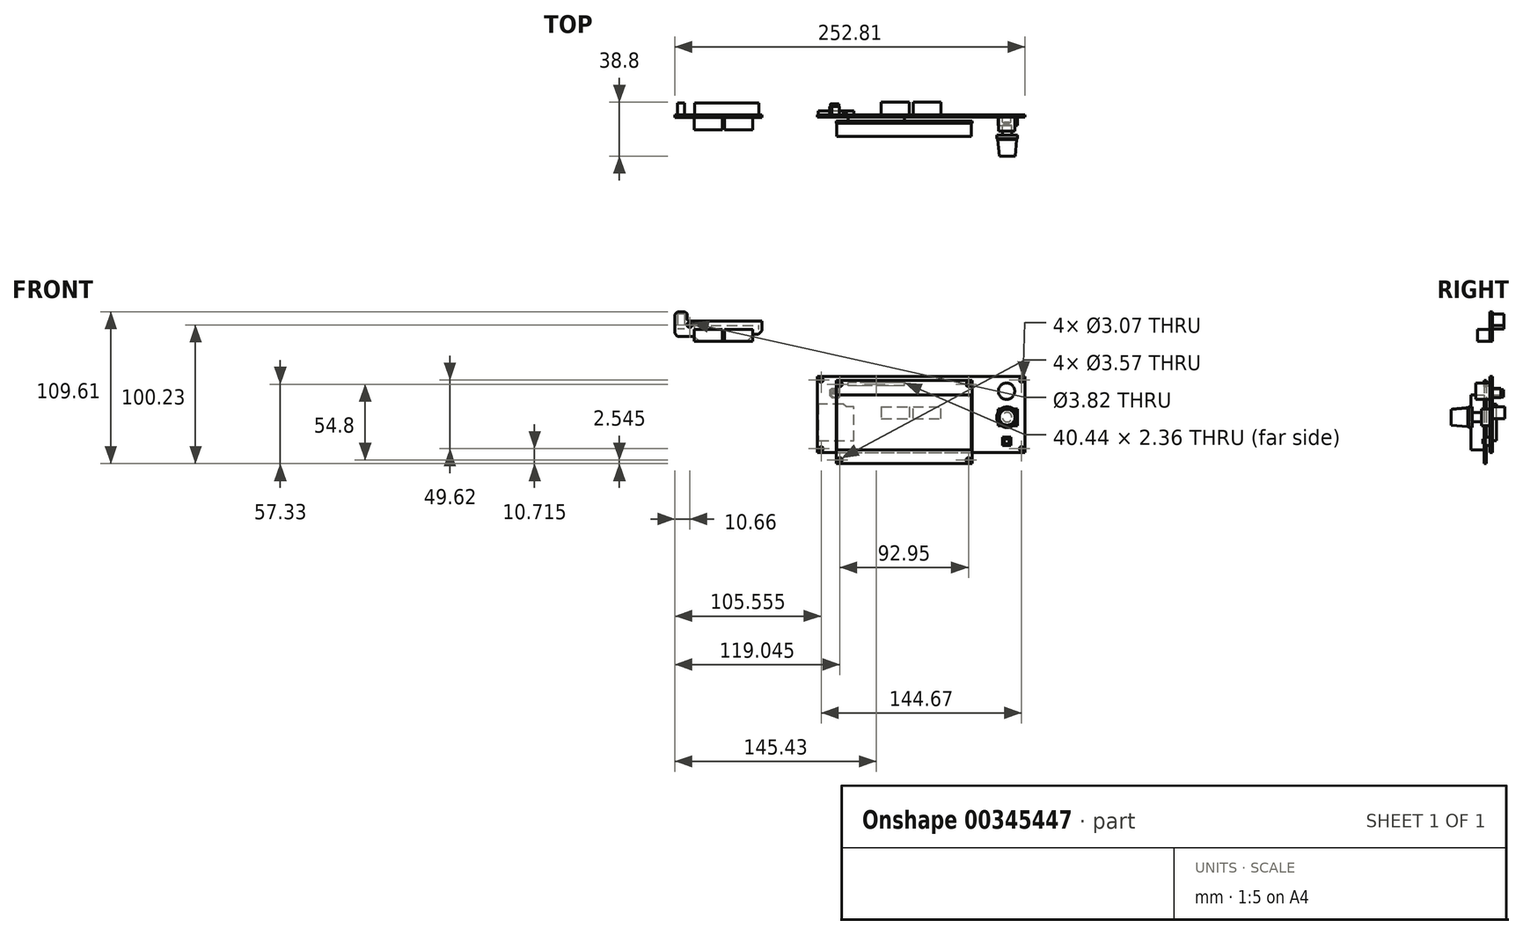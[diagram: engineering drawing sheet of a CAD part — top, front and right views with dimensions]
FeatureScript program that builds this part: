
annotation { "Feature Type Name" : "Feature", "Feature Type Description" : "" }
export const myFeature = defineFeature(function(context is Context, id is Id, definition is map)
    precondition{}
    {
        {
            var Q0;
            Q0=qCreatedBy(makeId("Front.planeOp"),FACE);
            var sketch = newSketch(context, id + "F0", { "sketchPlane" : qUnion([Q0])});
            skLineSegment(sketch, "E0.bottom", {"start": v(0, 0) * mm, "end": v(150.07, 0) * mm});
            skLineSegment(sketch, "E0.top", {"start": v(0, -55.1) * mm, "end": v(150.07, -55.1) * mm});
            skLineSegment(sketch, "E0.left", {"start": v(0, 0) * mm, "end": v(0, -55.1) * mm});
            skLineSegment(sketch, "E0.right", {"start": v(150.07, 0) * mm, "end": v(150.07, -55.1) * mm});
            skLineSegment(sketch, "E1", {"start": v(0, -2.7) * mm, "end": v(150.07, -2.7) * mm, "construction": true});
            skLineSegment(sketch, "E2", {"start": v(0, -52.33) * mm, "end": v(150.07, -52.32) * mm, "construction": true});
            skLineSegment(sketch, "E3", {"start": v(2.81, 0) * mm, "end": v(2.82, -55.1) * mm, "construction": true});
            skLineSegment(sketch, "E4", {"start": v(147.49, 0) * mm, "end": v(147.49, -55.1) * mm, "construction": true});
            skCircle(sketch, "E5", {"center": v(2.81, -2.7) * mm, "radius": 1.53 * mm});
            skCircle(sketch, "E6", {"center": v(2.81, -52.33) * mm, "radius": 1.53 * mm});
            skCircle(sketch, "E7", {"center": v(147.49, -2.7) * mm, "radius": 1.53 * mm});
            skCircle(sketch, "E8", {"center": v(147.49, -52.32) * mm, "radius": 1.53 * mm});
            skSolve(sketch);
        }
        {
            var Q0;
            Q0 = qSketchRegion(id + "F0", true);
            extrude(context, id + "F1", {"entities" : qUnion([Q0]), "depth" : 1.63 * mm});
        }
        {
            var Q0;
            Q0=makeQuery(id+"F1.opExtrude","CAP_FACE",FACE,{"disambiguationData":[OSD([sQuery(id+"F0.wireOp",EDGE,"E0.bottom"),sQuery(id+"F0.wireOp",EDGE,"E0.top"),sQuery(id+"F0.wireOp",EDGE,"E0.left"),sQuery(id+"F0.wireOp",EDGE,"E0.right")])],"isStart":false});
            cPlane(context, id + "F2", {"entities" : qUnion([Q0]), "cplaneType" : CPlaneType.OFFSET, "offset" : 2.7 * mm, "width" : 150 * mm, "height" : 150 * mm});
        }
        {
            var Q0;
            Q0=qCreatedBy(id+"F2.planeOp",FACE);
            var sketch = newSketch(context, id + "F3", { "sketchPlane" : qUnion([Q0])});
            skLineSegment(sketch, "E9.bottom", {"start": v(13.62, -3.08) * mm, "end": v(111.77, -3.08) * mm});
            skLineSegment(sketch, "E9.top", {"start": v(13.62, -63.04) * mm, "end": v(111.77, -63.04) * mm});
            skLineSegment(sketch, "E9.left", {"start": v(13.62, -3.08) * mm, "end": v(13.62, -63.04) * mm});
            skLineSegment(sketch, "E9.right", {"start": v(111.77, -3.08) * mm, "end": v(111.77, -63.04) * mm});
            skLineSegment(sketch, "E10.bottom", {"start": v(16.3, -5.7) * mm, "end": v(109.26, -5.7) * mm, "construction": true});
            skLineSegment(sketch, "E10.top", {"start": v(16.3, -60.5) * mm, "end": v(109.26, -60.5) * mm, "construction": true});
            skLineSegment(sketch, "E10.left", {"start": v(16.3, -5.7) * mm, "end": v(16.3, -60.5) * mm, "construction": true});
            skLineSegment(sketch, "E10.right", {"start": v(109.26, -5.7) * mm, "end": v(109.26, -60.5) * mm, "construction": true});
            skCircle(sketch, "E11", {"center": v(16.3, -5.7) * mm, "radius": 1.78 * mm});
            skCircle(sketch, "E12", {"center": v(109.26, -5.7) * mm, "radius": 1.78 * mm});
            skCircle(sketch, "E13", {"center": v(16.3, -60.5) * mm, "radius": 1.78 * mm});
            skCircle(sketch, "E14", {"center": v(109.26, -60.5) * mm, "radius": 1.78 * mm});
            skSolve(sketch);
        }
        {
            var Q0;
            Q0 = qSketchRegion(id + "F3", true);
            extrude(context, id + "F4", {"entities" : qUnion([Q0]), "depth" : 1.62 * mm});
        }
        {
            var Q0;
            Q0=makeQuery(id+"F4.opExtrude","CAP_FACE",FACE,{"disambiguationData":[OSD([sQuery(id+"F3.wireOp",EDGE,"E9.bottom"),sQuery(id+"F3.wireOp",EDGE,"E9.top"),sQuery(id+"F3.wireOp",EDGE,"E9.left"),sQuery(id+"F3.wireOp",EDGE,"E9.right")])],"isStart":false});
            var sketch = newSketch(context, id + "F5", { "sketchPlane" : qUnion([Q0])});
            skLineSegment(sketch, "E15", {"start": v(62.7, -3.08) * mm, "end": v(62.7, -63.04) * mm, "construction": true});
            skLineSegment(sketch, "E16.bottom", {"start": v(14.18, -13.36) * mm, "end": v(111.2, -13.36) * mm});
            skLineSegment(sketch, "E16.top", {"start": v(14.19, -53.18) * mm, "end": v(111.2, -53.18) * mm});
            skLineSegment(sketch, "E16.left", {"start": v(14.19, -13.36) * mm, "end": v(14.19, -53.18) * mm});
            skLineSegment(sketch, "E16.right", {"start": v(111.2, -13.36) * mm, "end": v(111.2, -53.18) * mm});
            skCircle(sketch, "E17", {"center": v(62.7, -33.06) * mm, "radius": 48.5 * mm, "construction": true});
            skSolve(sketch);
        }
        {
            var Q0;
            Q0 = qSketchRegion(id + "F5", true);
            extrude(context, id + "F6", {"entities" : qUnion([Q0]), "operationType" : NewBodyOperationType.ADD, "depth" : 9.45 * mm});
        }
        {
            var Q0;
            Q0=makeQuery(id+"F1.opExtrude","CAP_FACE",FACE,{"disambiguationData":[OSD([sQuery(id+"F0.wireOp",EDGE,"E0.bottom"),sQuery(id+"F0.wireOp",EDGE,"E0.top"),sQuery(id+"F0.wireOp",EDGE,"E0.left"),sQuery(id+"F0.wireOp",EDGE,"E0.right")])],"isStart":false});
            var sketch = newSketch(context, id + "F7", { "sketchPlane" : qUnion([Q0])});
            skLineSegment(sketch, "E18.bottom", {"start": v(133.8, -43.96) * mm, "end": v(139.76, -43.96) * mm});
            skLineSegment(sketch, "E18.top", {"start": v(133.8, -49.92) * mm, "end": v(139.76, -49.92) * mm});
            skLineSegment(sketch, "E18.left", {"start": v(133.8, -43.96) * mm, "end": v(133.8, -49.92) * mm});
            skLineSegment(sketch, "E18.right", {"start": v(139.76, -43.96) * mm, "end": v(139.76, -49.92) * mm});
            skCircle(sketch, "E19", {"center": v(136.78, -46.94) * mm, "radius": 2.98 * mm, "construction": true});
            skSolve(sketch);
        }
        {
            var Q0;
            Q0 = qSketchRegion(id + "F7", true);
            extrude(context, id + "F8", {"entities" : qUnion([Q0]), "operationType" : NewBodyOperationType.ADD, "depth" : 3.55 * mm});
        }
        {
            var Q0;
            Q0=makeQuery(id+"F8.opExtrude","CAP_FACE",FACE,{"disambiguationData":[OSD([sQuery(id+"F7.wireOp",EDGE,"E18.bottom"),sQuery(id+"F7.wireOp",EDGE,"E18.top"),sQuery(id+"F7.wireOp",EDGE,"E18.left"),sQuery(id+"F7.wireOp",EDGE,"E18.right")])],"isStart":false});
            var sketch = newSketch(context, id + "F9", { "sketchPlane" : qUnion([Q0])});
            skLineSegment(sketch, "E20", {"start": v(133.8, -43.96) * mm, "end": v(139.76, -49.92) * mm, "construction": true});
            skCircle(sketch, "E21", {"center": v(136.78, -46.94) * mm, "radius": 1.76 * mm});
            skSolve(sketch);
        }
        {
            var Q0;
            Q0 = qSketchRegion(id + "F9", true);
            extrude(context, id + "F10", {"entities" : qUnion([Q0]), "operationType" : NewBodyOperationType.ADD, "depth" : 1.57 * mm});
        }
        {
            var Q0;
            Q0=makeQuery(id+"F1.opExtrude","CAP_FACE",FACE,{"disambiguationData":[OSD([sQuery(id+"F0.wireOp",EDGE,"E0.bottom"),sQuery(id+"F0.wireOp",EDGE,"E0.top"),sQuery(id+"F0.wireOp",EDGE,"E0.left"),sQuery(id+"F0.wireOp",EDGE,"E0.right"),sQuery(id+"F0.wireOp",EDGE,"E5"),sQuery(id+"F0.wireOp",EDGE,"E6"),sQuery(id+"F0.wireOp",EDGE,"E7"),sQuery(id+"F0.wireOp",EDGE,"E8")])],"isStart":false});
            var sketch = newSketch(context, id + "F11", { "sketchPlane" : qUnion([Q0])});
            skLineSegment(sketch, "E22.bottom", {"start": v(130.73, -23.6) * mm, "end": v(144.54, -23.6) * mm});
            skLineSegment(sketch, "E22.top", {"start": v(130.73, -35.51) * mm, "end": v(144.54, -35.51) * mm});
            skLineSegment(sketch, "E22.left", {"start": v(130.73, -23.6) * mm, "end": v(130.73, -35.51) * mm});
            skLineSegment(sketch, "E22.right", {"start": v(144.54, -23.6) * mm, "end": v(144.54, -35.51) * mm});
            skSolve(sketch);
        }
        {
            var Q0;
            Q0 = qSketchRegion(id + "F11", true);
            extrude(context, id + "F12", {"entities" : qUnion([Q0]), "operationType" : NewBodyOperationType.ADD, "depth" : 6.04 * mm});
        }
        {
            var Q0;
            Q0=makeQuery(id+"F12.opExtrude","CAP_FACE",FACE,{"disambiguationData":[OSD([sQuery(id+"F11.wireOp",EDGE,"E22.bottom"),sQuery(id+"F11.wireOp",EDGE,"E22.top"),sQuery(id+"F11.wireOp",EDGE,"E22.left"),sQuery(id+"F11.wireOp",EDGE,"E22.right")])],"isStart":false});
            var sketch = newSketch(context, id + "F13", { "sketchPlane" : qUnion([Q0])});
            skLineSegment(sketch, "E23", {"start": v(130.73, -29.55) * mm, "end": v(144.54, -29.55) * mm, "construction": true});
            skCircle(sketch, "E24", {"center": v(137.11, -29.55) * mm, "radius": 3.41 * mm});
            skSolve(sketch);
        }
        {
            var Q0;
            Q0 = qSketchRegion(id + "F13", true);
            extrude(context, id + "F14", {"entities" : qUnion([Q0]), "operationType" : NewBodyOperationType.ADD, "depth" : 6.86 * mm});
        }
        {
            var Q0;
            Q0=sQuery(id+"F13.wireOp",EDGE,"E23");
            cPoint(context, id + "F15", {"entities" : qUnion([Q0]), "parameter" : 0.5});
        }
        {
            var Q0;
            Q0=qCreatedBy(makeId("Top.planeOp"),FACE);
            var Q1;
            Q1 = qCreatedBy(id + "F15" ,VERTEX);
            cPlane(context, id + "F16", {"entities" : qUnion([Q0, Q1]), "cplaneType" : CPlaneType.PLANE_POINT, "offset" : 25 * mm, "width" : 150 * mm, "height" : 150 * mm});
        }
        {
            var Q0;
            Q0=qCreatedBy(id+"F16.planeOp",FACE);
            var sketch = newSketch(context, id + "F17", { "sketchPlane" : qUnion([Q0])});
            skLineSegment(sketch, "E25.0", {"start": v(140.52, -14.53) * mm, "end": v(133.7, -14.53) * mm, "construction": true});
            skLineSegment(sketch, "E26", {"start": v(137.11, -14.53) * mm, "end": v(137.11, -29.65) * mm});
            skLineSegment(sketch, "E27", {"start": v(137.11, -29.65) * mm, "end": v(142.84, -29.65) * mm});
            skLineSegment(sketch, "E28", {"start": v(142.84, -29.65) * mm, "end": v(143.96, -17.58) * mm});
            skLineSegment(sketch, "E29", {"start": v(143.96, -17.58) * mm, "end": v(144.6, -16.95) * mm});
            skLineSegment(sketch, "E30", {"start": v(144.6, -16.95) * mm, "end": v(144.6, -14.53) * mm});
            skLineSegment(sketch, "E31", {"start": v(144.6, -14.53) * mm, "end": v(137.11, -14.53) * mm});
            skSolve(sketch);
        }
        {
            var Q0;
            Q0 = qSketchRegion(id + "F17", true);
            var Q1;
            Q1=sQuery(id+"F17.wireOp",EDGE,"E26");
            revolve(context, id + "F18", {"operationType" : NewBodyOperationType.ADD, "entities" : qUnion([Q0]), "axis" : qUnion([Q1]), "revolveType" : RevolveType.FULL});
        }
        {
            var Q0;
            Q0=makeQuery(id+"F1.opExtrude","CAP_FACE",FACE,{"disambiguationData":[OSD([sQuery(id+"F0.wireOp",EDGE,"E0.bottom"),sQuery(id+"F0.wireOp",EDGE,"E0.top"),sQuery(id+"F0.wireOp",EDGE,"E0.left"),sQuery(id+"F0.wireOp",EDGE,"E0.right"),sQuery(id+"F0.wireOp",EDGE,"E5"),sQuery(id+"F0.wireOp",EDGE,"E6"),sQuery(id+"F0.wireOp",EDGE,"E7"),sQuery(id+"F0.wireOp",EDGE,"E8")])],"isStart":false});
            var sketch = newSketch(context, id + "F19", { "sketchPlane" : qUnion([Q0])});
            skCircle(sketch, "E32", {"center": v(136.68, -10.73) * mm, "radius": 5.9 * mm});
            skSolve(sketch);
        }
        {
            var Q0;
            Q0 = qSketchRegion(id + "F19", true);
            extrude(context, id + "F20", {"entities" : qUnion([Q0]), "operationType" : NewBodyOperationType.ADD, "depth" : 10.15 * mm});
        }
        {
            var Q0;
            Q0=makeQuery(id+"F1.opExtrude","CAP_FACE",FACE,{"disambiguationData":[OSD([sQuery(id+"F0.wireOp",EDGE,"E0.bottom"),sQuery(id+"F0.wireOp",EDGE,"E0.top"),sQuery(id+"F0.wireOp",EDGE,"E0.left"),sQuery(id+"F0.wireOp",EDGE,"E0.right"),sQuery(id+"F0.wireOp",EDGE,"E5"),sQuery(id+"F0.wireOp",EDGE,"E6"),sQuery(id+"F0.wireOp",EDGE,"E7"),sQuery(id+"F0.wireOp",EDGE,"E8")])],"isStart":true});
            var sketch = newSketch(context, id + "F21", { "sketchPlane" : qUnion([Q0])});
            skLineSegment(sketch, "E33", {"start": v(-0.8, -46.57) * mm, "end": v(-26.48, -46.57) * mm});
            skLineSegment(sketch, "E34", {"start": v(-26.48, -46.57) * mm, "end": v(-26.48, -22.15) * mm});
            skLineSegment(sketch, "E35", {"start": v(-26.48, -22.15) * mm, "end": v(-21.02, -22.15) * mm});
            skLineSegment(sketch, "E36", {"start": v(-21.02, -22.15) * mm, "end": v(-18.87, -20) * mm});
            skLineSegment(sketch, "E37", {"start": v(-18.87, -20) * mm, "end": v(-0.8, -20) * mm});
            skLineSegment(sketch, "E38", {"start": v(-0.8, -20) * mm, "end": v(-0.8, -46.57) * mm});
            skSolve(sketch);
        }
        {
            var Q0;
            Q0 = qSketchRegion(id + "F21", true);
            extrude(context, id + "F22", {"entities" : qUnion([Q0]), "operationType" : NewBodyOperationType.ADD, "depth" : 2.91 * mm});
        }
        {
            var Q0;
            Q0=makeQuery(id+"F1.opExtrude","CAP_FACE",FACE,{"disambiguationData":[OSD([sQuery(id+"F0.wireOp",EDGE,"E0.bottom"),sQuery(id+"F0.wireOp",EDGE,"E0.top"),sQuery(id+"F0.wireOp",EDGE,"E0.left"),sQuery(id+"F0.wireOp",EDGE,"E0.right"),sQuery(id+"F0.wireOp",EDGE,"E5"),sQuery(id+"F0.wireOp",EDGE,"E6"),sQuery(id+"F0.wireOp",EDGE,"E7"),sQuery(id+"F0.wireOp",EDGE,"E8")])],"isStart":true});
            var sketch = newSketch(context, id + "F23", { "sketchPlane" : qUnion([Q0])});
            skLineSegment(sketch, "E39", {"start": v(-15.96, -11.92) * mm, "end": v(-9.02, -11.92) * mm, "construction": true});
            skLineSegment(sketch, "E40", {"start": v(-9.02, -11.92) * mm, "end": v(-9.02, -10.05) * mm});
            skLineSegment(sketch, "E41", {"start": v(-9.02, -10.05) * mm, "end": v(-10.48, -8.6) * mm});
            skLineSegment(sketch, "E42", {"start": v(-10.48, -8.6) * mm, "end": v(-15.96, -8.6) * mm});
            skLineSegment(sketch, "E43", {"start": v(-15.96, -8.6) * mm, "end": v(-15.96, -11.92) * mm});
            skLineSegment(sketch, "E44.MirrorCS", {"start": v(-15.96, -15.25) * mm, "end": v(-15.96, -11.92) * mm});
            skLineSegment(sketch, "E45.MirrorCS", {"start": v(-10.48, -15.25) * mm, "end": v(-15.96, -15.25) * mm});
            skLineSegment(sketch, "E46.MirrorCS", {"start": v(-9.02, -13.78) * mm, "end": v(-10.49, -15.25) * mm});
            skLineSegment(sketch, "E47.MirrorCS", {"start": v(-9.02, -11.92) * mm, "end": v(-9.02, -13.78) * mm});
            skSolve(sketch);
        }
        {
            var Q0;
            Q0 = qSketchRegion(id + "F23", true);
            extrude(context, id + "F24", {"entities" : qUnion([Q0]), "operationType" : NewBodyOperationType.ADD, "depth" : 6.15 * mm});
        }
        {
            var Q0;
            Q0=makeQuery(id+"F24.opExtrude","CAP_FACE",FACE,{"disambiguationData":[OSD([sQuery(id+"F23.wireOp",EDGE,"E40"),sQuery(id+"F23.wireOp",EDGE,"E41"),sQuery(id+"F23.wireOp",EDGE,"E42"),sQuery(id+"F23.wireOp",EDGE,"E43"),sQuery(id+"F23.wireOp",EDGE,"E44.MirrorCS"),sQuery(id+"F23.wireOp",EDGE,"E45.MirrorCS"),sQuery(id+"F23.wireOp",EDGE,"E46.MirrorCS"),sQuery(id+"F23.wireOp",EDGE,"E47.MirrorCS")])],"isStart":false});
            var sketch = newSketch(context, id + "F25", { "sketchPlane" : qUnion([Q0])});
            skLineSegment(sketch, "E48.0", {"start": v(-15.96, -11.92) * mm, "end": v(-9.02, -11.92) * mm, "construction": true});
            skCircle(sketch, "E49", {"center": v(-12.5, -11.92) * mm, "radius": 3 * mm});
            skLineSegment(sketch, "E50.bottom", {"start": v(-14.72, -11.4) * mm, "end": v(-12.5, -11.4) * mm});
            skLineSegment(sketch, "E50.left", {"start": v(-14.72, -11.4) * mm, "end": v(-14.72, -11.92) * mm});
            skLineSegment(sketch, "E51", {"start": v(-12.5, -11.92) * mm, "end": v(-12.5, -8.91) * mm, "construction": true});
            skLineSegment(sketch, "E52", {"start": v(-12.5, -11.92) * mm, "end": v(-12.5, -14.93) * mm, "construction": true});
            skLineSegment(sketch, "E53", {"start": v(-14.25, -9.48) * mm, "end": v(-13.82, -9.48) * mm});
            skLineSegment(sketch, "E54", {"start": v(-13.82, -9.48) * mm, "end": v(-13.82, -10.03) * mm});
            skLineSegment(sketch, "E55", {"start": v(-13.82, -10.03) * mm, "end": v(-12.5, -10.03) * mm});
            skLineSegment(sketch, "E56.MirrorCS", {"start": v(-14.72, -12.45) * mm, "end": v(-12.5, -12.45) * mm});
            skLineSegment(sketch, "E57.MirrorCS", {"start": v(-14.72, -12.45) * mm, "end": v(-14.72, -11.92) * mm});
            skLineSegment(sketch, "E58.MirrorCS", {"start": v(-11.16, -10.03) * mm, "end": v(-12.5, -10.03) * mm});
            skLineSegment(sketch, "E59.MirrorCS", {"start": v(-11.16, -9.48) * mm, "end": v(-11.16, -10.03) * mm});
            skLineSegment(sketch, "E60.MirrorCS", {"start": v(-10.73, -9.48) * mm, "end": v(-11.16, -9.48) * mm});
            skLineSegment(sketch, "E61.MirrorCS", {"start": v(-10.27, -11.4) * mm, "end": v(-12.5, -11.4) * mm});
            skLineSegment(sketch, "E62.MirrorCS", {"start": v(-10.27, -11.4) * mm, "end": v(-10.27, -11.92) * mm});
            skLineSegment(sketch, "E63.MirrorCS", {"start": v(-10.27, -12.45) * mm, "end": v(-10.27, -11.92) * mm});
            skLineSegment(sketch, "E64.MirrorCS", {"start": v(-10.27, -12.45) * mm, "end": v(-12.5, -12.45) * mm});
            skSolve(sketch);
        }
        {
            var Q0;
            Q0=makeQuery(id+"F25.imprint","IMPRINT",FACE,{"disambiguationData":[TD([[makeQuery(id+"F25.imprint","IMPRINT",EDGE,{"derivedFrom":sQuery(id+"F25.wireOp",EDGE,"E50.bottom")}),1.0]])]});
            extrude(context, id + "F26", {"entities" : qUnion([Q0]), "operationType" : NewBodyOperationType.ADD, "depth" : 1.85 * mm});
        }
        {
            var Q0;
            Q0=makeQuery(id+"F1.opExtrude","CAP_FACE",FACE,{"disambiguationData":[OSD([sQuery(id+"F0.wireOp",EDGE,"E0.bottom"),sQuery(id+"F0.wireOp",EDGE,"E0.top"),sQuery(id+"F0.wireOp",EDGE,"E0.left"),sQuery(id+"F0.wireOp",EDGE,"E0.right"),sQuery(id+"F0.wireOp",EDGE,"E5"),sQuery(id+"F0.wireOp",EDGE,"E6"),sQuery(id+"F0.wireOp",EDGE,"E7"),sQuery(id+"F0.wireOp",EDGE,"E8")])],"isStart":true});
            var sketch = newSketch(context, id + "F27", { "sketchPlane" : qUnion([Q0])});
            skLineSegment(sketch, "E65.bottom", {"start": v(-46.17, -22) * mm, "end": v(-66.44, -22) * mm});
            skLineSegment(sketch, "E65.top", {"start": v(-46.17, -30.71) * mm, "end": v(-66.44, -30.71) * mm});
            skLineSegment(sketch, "E65.left", {"start": v(-46.17, -22) * mm, "end": v(-46.17, -30.71) * mm});
            skLineSegment(sketch, "E65.right", {"start": v(-66.44, -22) * mm, "end": v(-66.44, -30.71) * mm});
            skLineSegment(sketch, "E66.bottom", {"start": v(-69.19, -30.71) * mm, "end": v(-89.46, -30.71) * mm});
            skLineSegment(sketch, "E66.top", {"start": v(-69.19, -22) * mm, "end": v(-89.46, -22) * mm});
            skLineSegment(sketch, "E66.left", {"start": v(-69.19, -30.71) * mm, "end": v(-69.19, -22) * mm});
            skLineSegment(sketch, "E66.right", {"start": v(-89.46, -30.71) * mm, "end": v(-89.46, -22) * mm});
            skLineSegment(sketch, "E67", {"start": v(-69.19, -30.71) * mm, "end": v(-66.44, -30.71) * mm, "construction": true});
            skLineSegment(sketch, "E68", {"start": v(-66.44, -22) * mm, "end": v(-69.19, -22) * mm, "construction": true});
            skSolve(sketch);
        }
        {
            var Q0;
            Q0 = qSketchRegion(id + "F27", true);
            extrude(context, id + "F28", {"entities" : qUnion([Q0]), "operationType" : NewBodyOperationType.ADD, "depth" : 9.15 * mm});
        }
        {
            var Q0;
            Q0=qCreatedBy(makeId("Front.planeOp"),FACE);
            var sketch = newSketch(context, id + "F29", { "sketchPlane" : qUnion([Q0])});
            skLineSegment(sketch, "E69", {"start": v(-40, 40) * mm, "end": v(-92.4, 40) * mm});
            skLineSegment(sketch, "E70", {"start": v(-93.99, 41.6) * mm, "end": v(-93.99, 45.24) * mm});
            skLineSegment(sketch, "E71", {"start": v(-93.99, 45.24) * mm, "end": v(-95.32, 46.57) * mm});
            skLineSegment(sketch, "E72", {"start": v(-95.32, 46.57) * mm, "end": v(-100.78, 46.57) * mm});
            skLineSegment(sketch, "E73", {"start": v(-100.78, 46.57) * mm, "end": v(-102.74, 44.6) * mm});
            skLineSegment(sketch, "E74", {"start": v(-102.74, 44.6) * mm, "end": v(-102.74, 30.85) * mm});
            skLineSegment(sketch, "E75", {"start": v(-102.74, 30.85) * mm, "end": v(-100.78, 28.89) * mm});
            skLineSegment(sketch, "E76", {"start": v(-100.78, 28.89) * mm, "end": v(-88.78, 28.89) * mm});
            skLineSegment(sketch, "E77", {"start": v(-88.78, 28.89) * mm, "end": v(-85.05, 25.16) * mm});
            skLineSegment(sketch, "E78", {"start": v(-85.05, 25.16) * mm, "end": v(-50.73, 25.16) * mm});
            skLineSegment(sketch, "E79", {"start": v(-50.73, 25.16) * mm, "end": v(-45.51, 30.38) * mm});
            skLineSegment(sketch, "E80", {"start": v(-42.42, 30.38) * mm, "end": v(-40, 32.8) * mm});
            skLineSegment(sketch, "E81", {"start": v(-40, 32.8) * mm, "end": v(-40, 40) * mm});
            skLineSegment(sketch, "E82", {"start": v(-45.51, 30.38) * mm, "end": v(-42.42, 30.38) * mm});
            skLineSegment(sketch, "E83", {"start": v(-100.78, 46.57) * mm, "end": v(-100.78, 28.89) * mm, "construction": true});
            skPoint(sketch, "E84.visualSharp", {"position": v(-93.99, 40) * mm});
            skArc(sketch, "E84.filletArc", {"start": v(-94, 41.6) * mm, "mid": v(-93.52, 40.47) * mm, "end": v(-92.4, 40) * mm});
            skCircle(sketch, "E85", {"center": v(-92.08, 37.19) * mm, "radius": 1.91 * mm});
            skLineSegment(sketch, "E86", {"start": v(-93.99, 41.6) * mm, "end": v(-93.99, 28.89) * mm, "construction": true});
            skSolve(sketch);
        }
        {
            var Q0;
            Q0 = qSketchRegion(id + "F29", true);
            extrude(context, id + "F30", {"entities" : qUnion([Q0]), "depth" : 1.74 * mm});
        }
        {
            var Q0;
            Q0=makeQuery(id+"F30.opExtrude","CAP_FACE",FACE,{"disambiguationData":[OSD([sQuery(id+"F29.wireOp",EDGE,"E69"),sQuery(id+"F29.wireOp",EDGE,"E70"),sQuery(id+"F29.wireOp",EDGE,"E71"),sQuery(id+"F29.wireOp",EDGE,"E72"),sQuery(id+"F29.wireOp",EDGE,"E73"),sQuery(id+"F29.wireOp",EDGE,"E74"),sQuery(id+"F29.wireOp",EDGE,"E75"),sQuery(id+"F29.wireOp",EDGE,"E76"),sQuery(id+"F29.wireOp",EDGE,"E77"),sQuery(id+"F29.wireOp",EDGE,"E78"),sQuery(id+"F29.wireOp",EDGE,"E79"),sQuery(id+"F29.wireOp",EDGE,"E80"),sQuery(id+"F29.wireOp",EDGE,"E81"),sQuery(id+"F29.wireOp",EDGE,"E82"),sQuery(id+"F29.wireOp",EDGE,"E84.filletArc"),sQuery(id+"F29.wireOp",EDGE,"E85")])],"isStart":false});
            var sketch = newSketch(context, id + "F31", { "sketchPlane" : qUnion([Q0])});
            skLineSegment(sketch, "E87.bottom", {"start": v(-68.54, 25.16) * mm, "end": v(-88.78, 25.16) * mm});
            skLineSegment(sketch, "E87.top", {"start": v(-68.54, 33.78) * mm, "end": v(-88.78, 33.78) * mm});
            skLineSegment(sketch, "E87.left", {"start": v(-68.54, 25.16) * mm, "end": v(-68.54, 33.78) * mm});
            skLineSegment(sketch, "E87.right", {"start": v(-88.78, 25.16) * mm, "end": v(-88.78, 33.78) * mm});
            skLineSegment(sketch, "E88.bottom", {"start": v(-66.85, 25.16) * mm, "end": v(-46.58, 25.16) * mm});
            skLineSegment(sketch, "E88.top", {"start": v(-66.85, 33.78) * mm, "end": v(-46.58, 33.78) * mm});
            skLineSegment(sketch, "E88.left", {"start": v(-66.85, 25.16) * mm, "end": v(-66.85, 33.78) * mm});
            skLineSegment(sketch, "E88.right", {"start": v(-46.58, 25.16) * mm, "end": v(-46.58, 33.78) * mm});
            skLineSegment(sketch, "E89", {"start": v(-68.54, 33.78) * mm, "end": v(-66.85, 33.78) * mm, "construction": true});
            skSolve(sketch);
        }
        {
            var Q0;
            Q0 = qSketchRegion(id + "F31", true);
            extrude(context, id + "F32", {"entities" : qUnion([Q0]), "operationType" : NewBodyOperationType.ADD, "depth" : 9.02 * mm});
        }
        {
            var Q0;
            Q0=makeQuery(id+"F30.opExtrude","CAP_FACE",FACE,{"disambiguationData":[OSD([sQuery(id+"F29.wireOp",EDGE,"E69"),sQuery(id+"F29.wireOp",EDGE,"E70"),sQuery(id+"F29.wireOp",EDGE,"E71"),sQuery(id+"F29.wireOp",EDGE,"E72"),sQuery(id+"F29.wireOp",EDGE,"E73"),sQuery(id+"F29.wireOp",EDGE,"E74"),sQuery(id+"F29.wireOp",EDGE,"E75"),sQuery(id+"F29.wireOp",EDGE,"E76"),sQuery(id+"F29.wireOp",EDGE,"E77"),sQuery(id+"F29.wireOp",EDGE,"E78"),sQuery(id+"F29.wireOp",EDGE,"E79"),sQuery(id+"F29.wireOp",EDGE,"E80"),sQuery(id+"F29.wireOp",EDGE,"E81"),sQuery(id+"F29.wireOp",EDGE,"E82"),sQuery(id+"F29.wireOp",EDGE,"E84.filletArc"),sQuery(id+"F29.wireOp",EDGE,"E85")])],"isStart":true});
            var sketch = newSketch(context, id + "F33", { "sketchPlane" : qUnion([Q0])});
            skLineSegment(sketch, "E90.bottom", {"start": v(95.85, 44.89) * mm, "end": v(100.83, 44.89) * mm});
            skLineSegment(sketch, "E90.top", {"start": v(95.85, 34.32) * mm, "end": v(100.83, 34.32) * mm});
            skLineSegment(sketch, "E90.left", {"start": v(95.85, 44.89) * mm, "end": v(95.85, 34.32) * mm});
            skLineSegment(sketch, "E90.right", {"start": v(100.83, 44.89) * mm, "end": v(100.83, 34.32) * mm});
            skLineSegment(sketch, "E91.bottom", {"start": v(88.33, 34.32) * mm, "end": v(42.1, 34.32) * mm});
            skLineSegment(sketch, "E91.top", {"start": v(88.33, 36.69) * mm, "end": v(42.1, 36.69) * mm});
            skLineSegment(sketch, "E91.left", {"start": v(88.33, 34.32) * mm, "end": v(88.33, 36.69) * mm});
            skLineSegment(sketch, "E91.right", {"start": v(42.1, 34.32) * mm, "end": v(42.1, 36.69) * mm});
            skLineSegment(sketch, "E92", {"start": v(88.33, 34.32) * mm, "end": v(95.85, 34.32) * mm, "construction": true});
            skSolve(sketch);
        }
        {
            var Q0;
            Q0 = qSketchRegion(id + "F33", true);
            extrude(context, id + "F34", {"entities" : qUnion([Q0]), "operationType" : NewBodyOperationType.ADD, "depth" : 8.52 * mm});
        }
        {
            var Q0;
            Q0=makeQuery(id+"F1.opExtrude","CAP_FACE",FACE,{"disambiguationData":[OSD([sQuery(id+"F0.wireOp",EDGE,"E0.bottom"),sQuery(id+"F0.wireOp",EDGE,"E0.top"),sQuery(id+"F0.wireOp",EDGE,"E0.left"),sQuery(id+"F0.wireOp",EDGE,"E0.right"),sQuery(id+"F0.wireOp",EDGE,"E5"),sQuery(id+"F0.wireOp",EDGE,"E6"),sQuery(id+"F0.wireOp",EDGE,"E7"),sQuery(id+"F0.wireOp",EDGE,"E8")])],"isStart":true});
            var sketch = newSketch(context, id + "F35", { "sketchPlane" : qUnion([Q0])});
            skLineSegment(sketch, "E93.bottom", {"start": v(-22.47, -4.53) * mm, "end": v(-62.9, -4.53) * mm});
            skLineSegment(sketch, "E93.top", {"start": v(-22.47, -6.9) * mm, "end": v(-62.9, -6.9) * mm});
            skLineSegment(sketch, "E93.left", {"start": v(-22.47, -4.53) * mm, "end": v(-22.47, -6.9) * mm});
            skLineSegment(sketch, "E93.right", {"start": v(-62.9, -4.53) * mm, "end": v(-62.9, -6.9) * mm});
            skSolve(sketch);
        }
        {
            var Q0;
            Q0 = qSketchRegion(id + "F35", true);
            var Q1;
            Q1=makeQuery(id+"F4.opExtrude","CAP_FACE",FACE,{"disambiguationData":[OSD([sQuery(id+"F3.wireOp",EDGE,"E9.bottom"),sQuery(id+"F3.wireOp",EDGE,"E9.top"),sQuery(id+"F3.wireOp",EDGE,"E9.left"),sQuery(id+"F3.wireOp",EDGE,"E9.right"),sQuery(id+"F3.wireOp",EDGE,"E11"),sQuery(id+"F3.wireOp",EDGE,"E12"),sQuery(id+"F3.wireOp",EDGE,"E13"),sQuery(id+"F3.wireOp",EDGE,"E14")])],"isStart":true});
            extrude(context, id + "F36", {"entities" : qUnion([Q0]), "operationType" : NewBodyOperationType.ADD, "endBound" : BoundingType.UP_TO_SURFACE, "oppositeDirection" : true, "endBoundEntityFace" : qUnion([Q1]), "depth" : 25 * mm});
        }
    });
